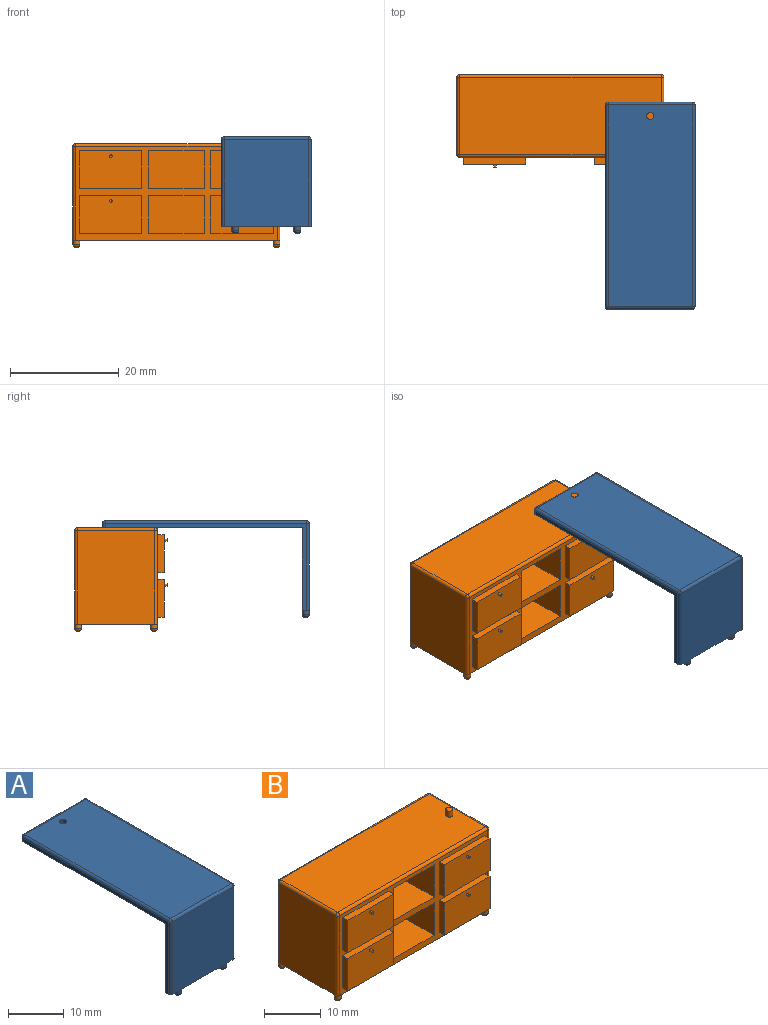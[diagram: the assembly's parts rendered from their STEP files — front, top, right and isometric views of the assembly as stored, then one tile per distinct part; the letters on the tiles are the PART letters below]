
ASSEMBLY  parts=2 mates=1
PART A: 29 faces, bbox 16.5x38.1x17.8 mm
  f0: plane 11.43x1.27mm, normal (0,0,-1), area 13.2mm2, adj f4,f9,f11,f13
  f1: plane 2.54x1.27mm, normal (0,0,-1), area 2.5mm2, adj f3,f4,f9,f11,f26
  f2: plane 2.54x1.27mm, normal (0,0,-1), area 2.5mm2, adj f4,f7,f9,f13,f22
  f3: plane 37.08x16mm, normal (1,0,0), area 39.9mm2, adj f1,f8,f9,f19,f21,f26
  f4: plane 16x15.49mm, normal (0,-1,0), area 247.9mm2, adj f0,f1,f2,f22,f24,f26
  f5: plane 15.49x0.76mm, normal (0,1,0), area 11.8mm2, adj f8,f16,f18,f21
  f6: plane 37.08x15.49mm, normal (0,0,1), area 573.3mm2, adj f10,f15,f16,f19,f24
  f7: plane 37.08x16mm, normal (-1,0,0), area 39.9mm2, adj f2,f8,f9,f15,f18,f22
  f8: plane 36.83x16.51mm, normal (0,0,-1), area 606.7mm2, adj f3,f5,f7,f9,f10,f18,f21
  f9: plane 16.51x15.24mm, normal (0,1,0), area 251.6mm2, adj f0,f1,f2,f3,f7,f8
  f10: cylinder r=0.64mm len=1.27mm, axis (0,0,1), area 5.1mm2, adj f6,f8
  f11: cylinder r=0.64mm len=1.27mm, axis (0,0,1), area 3mm2, adj f0,f1,f27
  f12: plane 0.25x0.25mm, normal (0,0,-1), area 0.1mm2, adj f27
  f13: cylinder r=0.64mm len=1.27mm, axis (0,0,1), area 3mm2, adj f0,f2,f28
  f14: plane 0.25x0.25mm, normal (0,0,-1), area 0.1mm2, adj f28
  f15: cylinder r=0.51mm len=37.08mm, axis (0,-1,0), area 29.6mm2, adj f6,f7,f17,f23
  f16: cylinder r=0.51mm len=15.49mm, axis (1,0,0), area 12.4mm2, adj f5,f6,f17,f20
  f17: sphere r=0.51mm, area 0.4mm2, adj f15,f16,f18
  f18: cylinder r=0.51mm len=0.76mm, axis (0,0,1), area 0.6mm2, adj f5,f7,f8,f17
  f19: cylinder r=0.51mm len=37.08mm, axis (0,1,0), area 29.6mm2, adj f3,f6,f20,f25
  f20: sphere r=0.51mm, area 0.4mm2, adj f16,f19,f21
  f21: cylinder r=0.51mm len=0.76mm, axis (0,0,-1), area 0.6mm2, adj f3,f5,f8,f20
  f22: cylinder r=0.51mm len=16mm, axis (0,0,-1), area 12.8mm2, adj f2,f4,f7,f23
  f23: sphere r=0.51mm, area 0.4mm2, adj f15,f22,f24
  f24: cylinder r=0.51mm len=15.49mm, axis (-1,0,0), area 12.4mm2, adj f4,f6,f23,f25
  f25: sphere r=0.51mm, area 0.4mm2, adj f19,f24,f26
  f26: cylinder r=0.51mm len=16mm, axis (0,0,1), area 12.8mm2, adj f1,f3,f4,f25
  f27: torus R=0.13mm, axis (0,0,-1), area 2.3mm2, adj f11,f12
  f28: torus R=0.13mm, axis (0,0,-1), area 2.3mm2, adj f13,f14
PART B: 74 faces, bbox 38.1x17x20.3 mm
  f0: plane 0.64x0.64mm, normal (0,0,-1), area 0mm2, adj f4,f7,f56,f69
  f1: plane 0.64x0.64mm, normal (0,0,-1), area 0mm2, adj f7,f9,f54,f65
  f2: plane 0.64x0.64mm, normal (0,0,-1), area 0mm2, adj f5,f9,f52,f60
  f3: plane 38.1x15.24mm, normal (0,0,-1), area 575.2mm2, adj f4,f5,f7,f9,f50,f52,f54,f56
  f4: plane 37.08x17.27mm, normal (0,-1,0), area 179.2mm2, adj f0,f3,f6,f12,f13,f14,f15,f17
  f5: plane 17.27x14.22mm, normal (-1,0,0), area 245.7mm2, adj f2,f3,f6,f60,f62,f64
  f6: plane 0.64x0.64mm, normal (0,0,-1), area 0mm2, adj f4,f5,f50,f64
  f7: plane 17.27x14.22mm, normal (1,0,0), area 245.7mm2, adj f0,f1,f3,f65,f67,f69
  f8: plane 37.08x14.22mm, normal (0,0,1), area 526.2mm2, adj f10,f58,f59,f62,f67
  f9: plane 37.08x17.27mm, normal (0,1,0), area 640.5mm2, adj f1,f2,f3,f59,f60,f65
  f10: cylinder r=0.64mm len=1.27mm, axis (0,0,-1), area 5.1mm2, adj f8,f11
  f11: plane 1.27x1.27mm, normal (0,0,1), area 1.3mm2, adj f10
  f12: plane 13.97x6.99mm, normal (1,0,0), area 97.6mm2, adj f4,f13,f15,f16
  f13: plane 13.97x10.16mm, normal (0,0,1), area 141.9mm2, adj f4,f12,f14,f16
  f14: plane 13.97x6.99mm, normal (-1,0,0), area 97.6mm2, adj f4,f13,f15,f16
  f15: plane 13.97x10.16mm, normal (0,0,-1), area 141.9mm2, adj f4,f12,f14,f16
  f16: plane 10.16x6.99mm, normal (0,-1,0), area 71mm2, adj f12,f13,f14,f15
  f17: plane 13.97x6.99mm, normal (1,0,0), area 97.6mm2, adj f4,f18,f20,f21
  f18: plane 13.97x10.16mm, normal (0,0,1), area 141.9mm2, adj f4,f17,f19,f21
  f19: plane 13.97x6.99mm, normal (-1,0,0), area 97.6mm2, adj f4,f18,f20,f21
  f20: plane 13.97x10.16mm, normal (0,0,-1), area 141.9mm2, adj f4,f17,f19,f21
  f21: plane 10.16x6.99mm, normal (0,-1,0), area 71mm2, adj f17,f18,f19,f20
  f22: plane 11.43x1.27mm, normal (0,0,1), area 14.5mm2, adj f4,f23,f25,f26
  f23: plane 6.99x1.27mm, normal (-1,0,0), area 8.9mm2, adj f4,f22,f24,f26
  f24: plane 11.43x1.27mm, normal (0,0,-1), area 14.5mm2, adj f4,f23,f25,f26
  f25: plane 6.99x1.27mm, normal (1,0,0), area 8.9mm2, adj f4,f22,f24,f26
  f26: plane 11.43x6.99mm, normal (0,-1,0), area 79.6mm2, adj f22,f23,f24,f25,f28
  f27: plane 0.51x0.51mm, normal (0,-1,0), area 0.2mm2, adj f28
  f28: cylinder r=0.25mm len=0.51mm, axis (0,1,0), area 0.8mm2, adj f26,f27
  f29: plane 6.99x1.27mm, normal (-1,0,0), area 8.9mm2, adj f4,f30,f32,f33
  f30: plane 11.43x1.27mm, normal (0,0,-1), area 14.5mm2, adj f4,f29,f31,f33
  f31: plane 6.99x1.27mm, normal (1,0,0), area 8.9mm2, adj f4,f30,f32,f33
  f32: plane 11.43x1.27mm, normal (0,0,1), area 14.5mm2, adj f4,f29,f31,f33
  f33: plane 11.43x6.99mm, normal (0,-1,0), area 79.6mm2, adj f29,f30,f31,f32,f35
  f34: plane 0.51x0.51mm, normal (0,-1,0), area 0.2mm2, adj f35
  f35: cylinder r=0.25mm len=0.51mm, axis (0,1,0), area 0.8mm2, adj f33,f34
  f36: plane 6.99x1.27mm, normal (-1,0,0), area 8.9mm2, adj f4,f37,f39,f40
  f37: plane 11.43x1.27mm, normal (0,0,-1), area 14.5mm2, adj f4,f36,f38,f40
  f38: plane 6.99x1.27mm, normal (1,0,0), area 8.9mm2, adj f4,f37,f39,f40
  f39: plane 11.43x1.27mm, normal (0,0,1), area 14.5mm2, adj f4,f36,f38,f40
  f40: plane 11.43x6.99mm, normal (0,-1,0), area 79.6mm2, adj f36,f37,f38,f39,f42
  f41: plane 0.51x0.51mm, normal (0,-1,0), area 0.2mm2, adj f42
  f42: cylinder r=0.25mm len=0.51mm, axis (0,1,0), area 0.8mm2, adj f40,f41
  f43: plane 6.99x1.27mm, normal (-1,0,0), area 8.9mm2, adj f4,f44,f46,f47
  f44: plane 11.43x1.27mm, normal (0,0,-1), area 14.5mm2, adj f4,f43,f45,f47
  f45: plane 6.99x1.27mm, normal (1,0,0), area 8.9mm2, adj f4,f44,f46,f47
  f46: plane 11.43x1.27mm, normal (0,0,1), area 14.5mm2, adj f4,f43,f45,f47
  f47: plane 11.43x6.99mm, normal (0,-1,0), area 79.6mm2, adj f43,f44,f45,f46,f49
  f48: plane 0.51x0.51mm, normal (0,-1,0), area 0.2mm2, adj f49
  f49: cylinder r=0.25mm len=0.51mm, axis (0,1,0), area 0.8mm2, adj f47,f48
  f50: cylinder r=0.64mm len=1.27mm, axis (0,0,1), area 3mm2, adj f3,f6,f73
  f51: plane 0.25x0.25mm, normal (0,0,-1), area 0.1mm2, adj f73
  f52: cylinder r=0.64mm len=1.27mm, axis (0,0,1), area 3mm2, adj f2,f3,f72
  f53: plane 0.25x0.25mm, normal (0,0,-1), area 0.1mm2, adj f72
  f54: cylinder r=0.64mm len=1.27mm, axis (0,0,1), area 3mm2, adj f1,f3,f71
  f55: plane 0.25x0.25mm, normal (0,0,-1), area 0.1mm2, adj f71
  f56: cylinder r=0.64mm len=1.27mm, axis (0,0,1), area 3mm2, adj f0,f3,f70
  f57: plane 0.25x0.25mm, normal (0,0,-1), area 0.1mm2, adj f70
  f58: cylinder r=0.51mm len=37.08mm, axis (1,0,0), area 29.6mm2, adj f4,f8,f63,f68
  f59: cylinder r=0.51mm len=37.08mm, axis (-1,0,0), area 29.6mm2, adj f8,f9,f61,f66
  f60: cylinder r=0.51mm len=17.27mm, axis (0,0,-1), area 13.8mm2, adj f2,f5,f9,f61
  f61: sphere r=0.51mm, area 0.4mm2, adj f59,f60,f62
  f62: cylinder r=0.51mm len=14.22mm, axis (0,1,0), area 11.4mm2, adj f5,f8,f61,f63
  f63: sphere r=0.51mm, area 0.4mm2, adj f58,f62,f64
  f64: cylinder r=0.51mm len=17.27mm, axis (0,0,1), area 13.8mm2, adj f4,f5,f6,f63
  f65: cylinder r=0.51mm len=17.27mm, axis (0,0,1), area 13.8mm2, adj f1,f7,f9,f66
  f66: sphere r=0.51mm, area 0.4mm2, adj f59,f65,f67
  f67: cylinder r=0.51mm len=14.22mm, axis (0,1,0), area 11.4mm2, adj f7,f8,f66,f68
  f68: sphere r=0.51mm, area 0.4mm2, adj f58,f67,f69
  f69: cylinder r=0.51mm len=17.27mm, axis (0,0,-1), area 13.8mm2, adj f0,f4,f7,f68
  f70: torus R=0.13mm, axis (0,0,-1), area 2.3mm2, adj f56,f57
  f71: torus R=0.13mm, axis (0,0,-1), area 2.3mm2, adj f54,f55
  f72: torus R=0.13mm, axis (0,0,-1), area 2.3mm2, adj f52,f53
  f73: torus R=0.13mm, axis (0,0,-1), area 2.3mm2, adj f50,f51
PLACE A t=(-14.08,-23.14,2.54)mm
PLACE B at identity
MATE parallel A.f10 <-> B.f10  axis (0,0,1) through (-5.83,-7.62,19.05)mm
